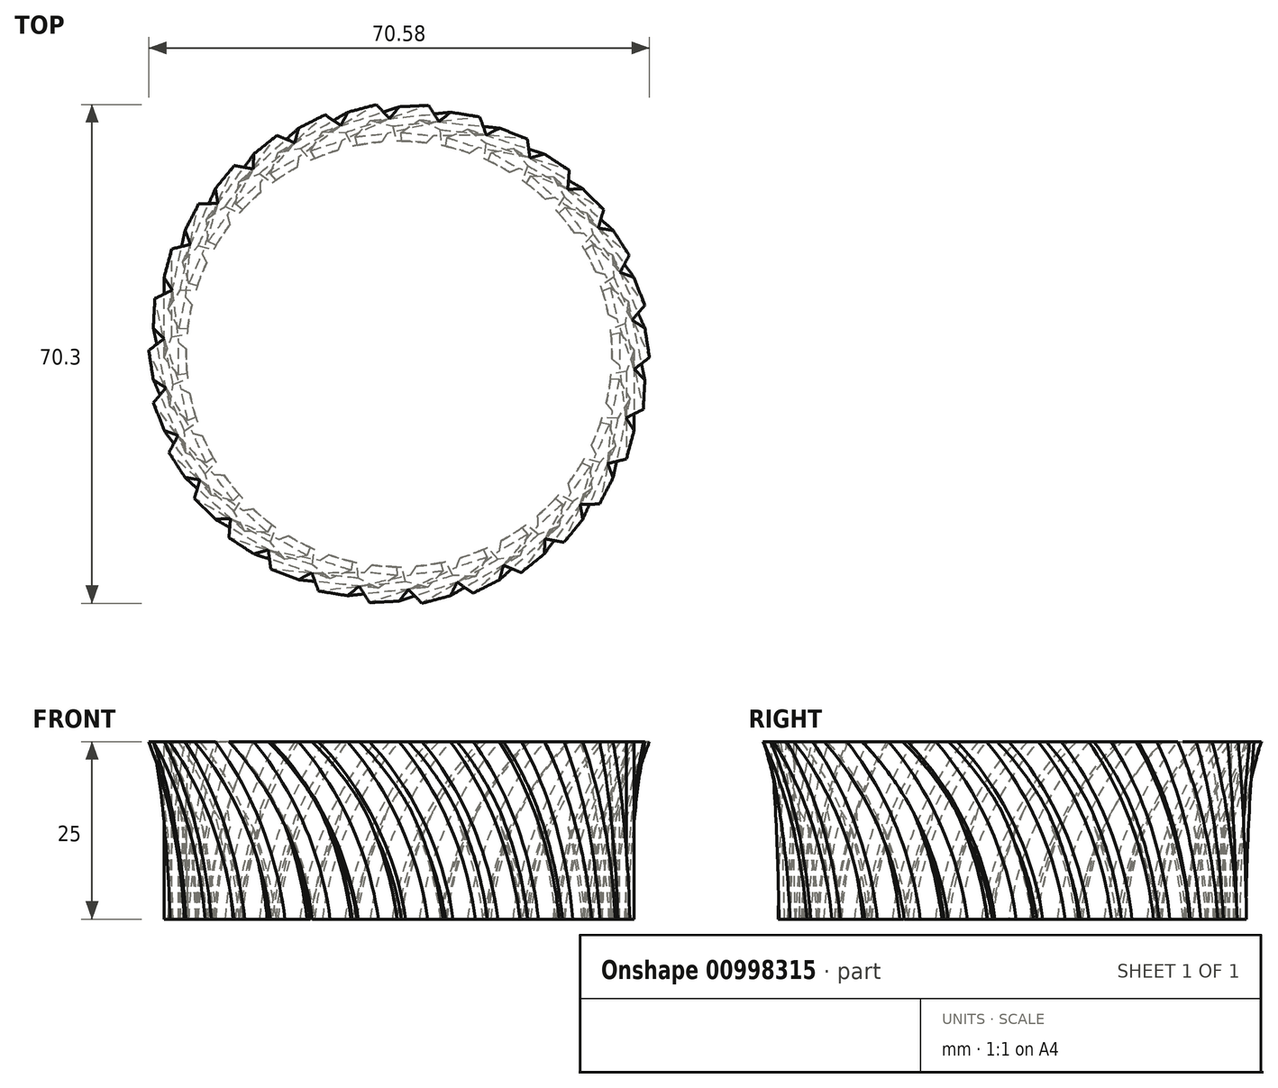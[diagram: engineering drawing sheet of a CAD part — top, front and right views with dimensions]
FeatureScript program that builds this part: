
annotation { "Feature Type Name" : "Feature", "Feature Type Description" : "" }
export const myFeature = defineFeature(function(context is Context, id is Id, definition is map)
    precondition{}
    {
        {
            var Q0;
            Q0=qCreatedBy(makeId("Top.planeOp"),FACE);
            var sketch = newSketch(context, id + "F0", { "sketchPlane" : qUnion([Q0])});
            skCircle(sketch, "E0.cCircle", {"center": v(-30, 0) * mm, "radius": 2.75 * mm, "construction": true});
            skLineSegment(sketch, "E0.0", {"start": v(-33.13, -0.55) * mm, "end": v(-32.04, 2.43) * mm});
            skLineSegment(sketch, "E0.1", {"start": v(-32.04, 2.43) * mm, "end": v(-28.91, 2.98) * mm});
            skLineSegment(sketch, "E0.2", {"start": v(-28.91, 2.98) * mm, "end": v(-26.87, 0.55) * mm});
            skLineSegment(sketch, "E0.3", {"start": v(-26.87, 0.55) * mm, "end": v(-27.96, -2.43) * mm});
            skLineSegment(sketch, "E0.4", {"start": v(-27.96, -2.43) * mm, "end": v(-31.09, -2.98) * mm});
            skLineSegment(sketch, "E0.5", {"start": v(-31.09, -2.98) * mm, "end": v(-33.13, -0.55) * mm});
            skPoint(sketch, "E0.0.midPoint", {"position": v(-32.58, 0.94) * mm});
            skLineSegment(sketch, "E1", {"start": v(-17.63, 1.82) * mm, "end": v(-17.63, -1.53) * mm});
            skLineSegment(sketch, "E2", {"start": v(-17.63, 1.82) * mm, "end": v(-28.91, 2.98) * mm});
            skLineSegment(sketch, "E3", {"start": v(-27.96, -2.43) * mm, "end": v(-17.63, -1.53) * mm});
            skSolve(sketch);
        }
        {
            var Q0;
            Q0=qCreatedBy(makeId("Right.planeOp"),FACE);
            cPlane(context, id + "F1", {"entities" : qUnion([Q0]), "cplaneType" : CPlaneType.OFFSET, "offset" : 30 * mm, "oppositeDirection" : true, "width" : 150 * mm, "height" : 150 * mm});
        }
        {
            var Q0;
            Q0=qCreatedBy(id+"F1.planeOp",FACE);
            var sketch = newSketch(context, id + "F2", { "sketchPlane" : qUnion([Q0])});
            skArc(sketch, "E4", {"start": v(13.17, 26.78) * mm, "mid": v(4.44, 14.45) * mm, "end": v(0, 0) * mm});
            skSolve(sketch);
        }
        {
            var Q0;
            Q0=qCreatedBy(makeId("Front.planeOp"),FACE);
            var sketch = newSketch(context, id + "F3", { "sketchPlane" : qUnion([Q0])});
            skLineSegment(sketch, "E5", {"start": v(0, 0) * mm, "end": v(0, 31.82) * mm});
            skSolve(sketch);
        }
        {
            var Q0;
            Q0 = qSketchRegion(id + "F0", true);
            var Q1;
            Q1 = qConstructionFilter(qBodyType(qCreatedBy(id + "F2" ,EDGE), BodyType.WIRE), ConstructionObject.NO);
            sweep(context, id + "F4", {"profiles" : qUnion([Q0]), "path" : qUnion([Q1])});
        }
        {
            var Q0;
            Q0=makeQuery(id+"F4.opSweep","SWEPT_BODY",BODY,{"disambiguationData":[OSD([sQuery(id+"F0.wireOp",EDGE,"E0.0"),sQuery(id+"F0.wireOp",EDGE,"E0.1"),sQuery(id+"F0.wireOp",EDGE,"E0.2"),sQuery(id+"F0.wireOp",EDGE,"E0.3"),sQuery(id+"F0.wireOp",EDGE,"E0.4"),sQuery(id+"F0.wireOp",EDGE,"E0.5"),sQuery(id+"F2.wireOp",EDGE,"E4")])]});
            var Q1;
            Q1=sQuery(id+"F3.wireOp",EDGE,"E5");
            circularPattern(context, id + "F5", {"operationType" : NewBodyOperationType.ADD, "entities" : qUnion([Q0]), "axis" : qUnion([Q1]), "angle" : 360 * degree, "instanceCount" : 30, "equalSpace" : true});
        }
        {
            var Q0;
            Q0=qCreatedBy(makeId("Top.planeOp"),FACE);
            var sketch = newSketch(context, id + "F6", { "sketchPlane" : qUnion([Q0])});
            skCircle(sketch, "E6", {"center": v(0, 0) * mm, "radius": 30 * mm});
            skSolve(sketch);
        }
        {
            var Q0;
            Q0 = qSketchRegion(id + "F6", true);
            extrude(context, id + "F7", {"entities" : qUnion([Q0]), "operationType" : NewBodyOperationType.ADD, "depth" : 25 * mm, "offsetDistance" : 25 * mm});
        }
        {
            var Q0;
            Q0=makeQuery(id+"F7.opExtrude","CAP_FACE",FACE,{"disambiguationData":[OSD([sQuery(id+"F6.wireOp",EDGE,"E6")])],"isStart":false});
            var sketch = newSketch(context, id + "F8", { "sketchPlane" : qUnion([Q0])});
            skCircle(sketch, "E7", {"center": v(0, 0) * mm, "radius": 86.14 * mm});
            skSolve(sketch);
        }
        {
            var Q0;
            Q0=makeQuery(id+"F8.imprint","IMPRINT",FACE,{"disambiguationData":[TD([[makeQuery(id+"F8.imprint","IMPRINT",EDGE,{"derivedFrom":sQuery(id+"F8.wireOp",EDGE,"E7")}),1.0]])]});
            var Q1;
            {var subQ0=sQuery(id+"F2.wireOp",EDGE,"E4");var subQ5=sQuery(id+"F6.wireOp",EDGE,"E6");var subQ6=makeQuery(id+"F7.opExtrude","CAP_FACE",FACE,{"disambiguationData":[OSD([subQ5])],"isStart":false});var subQ55=makeQuery(id+"F4.opSweep","SWEPT_FACE",FACE,{"disambiguationData":[OSD([sQuery(id+"F0.wireOp",EDGE,"E0.3"),subQ0])]});Q1=makeQuery(id+"F8.imprint","IMPRINT",FACE,{"disambiguationData":[TD([[makeQuery(id+"F8.imprint","IMPRINT",EDGE,{"derivedFrom":makeQuery(id+"F7.boolean.opBoolean","INTERSECT",EDGE,{"derivedFrom":[subQ55,subQ6]})}),1.0]])]});}
            extrude(context, id + "F9", {"entities" : qUnion([Q0, Q1]), "operationType" : NewBodyOperationType.REMOVE, "depth" : 25 * mm, "offsetDistance" : 25 * mm});
        }
    });
